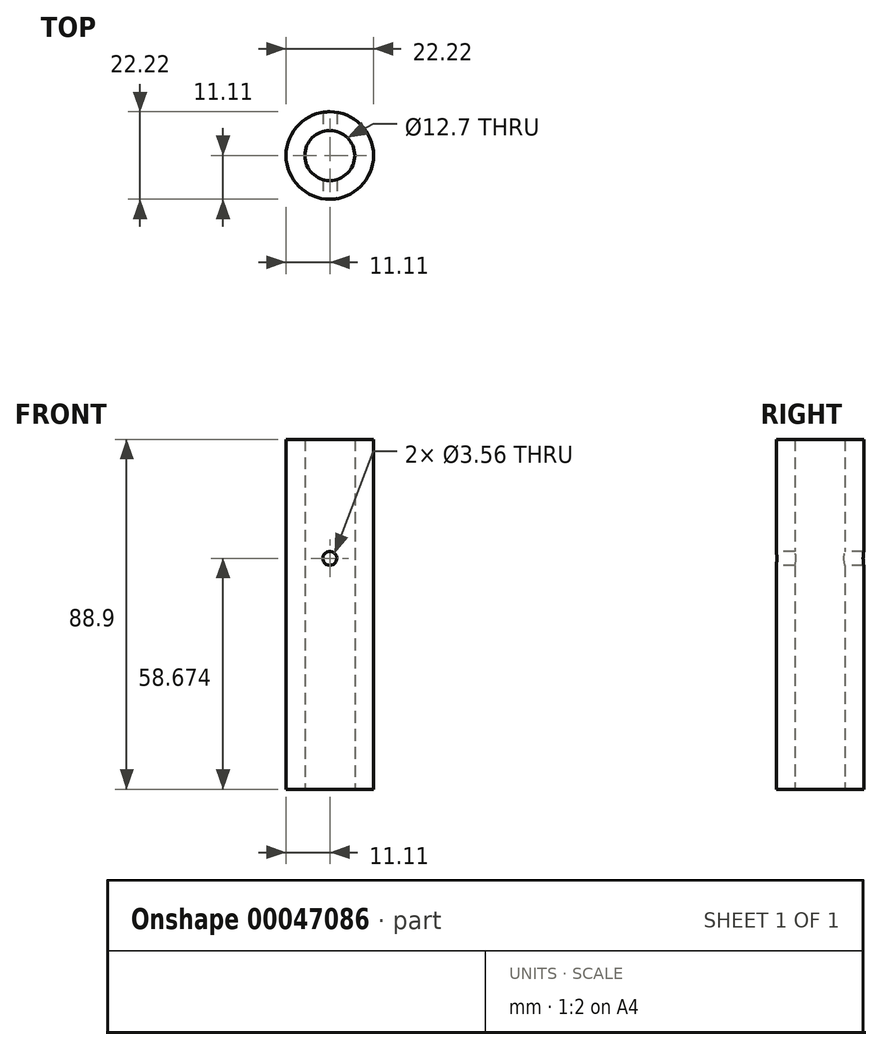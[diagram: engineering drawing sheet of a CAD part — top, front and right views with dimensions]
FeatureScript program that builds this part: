
annotation { "Feature Type Name" : "Feature", "Feature Type Description" : "" }
export const myFeature = defineFeature(function(context is Context, id is Id, definition is map)
    precondition{}
    {
        {
            var Q0;
            Q0=qCreatedBy(makeId("Top.planeOp"),FACE);
            var sketch = newSketch(context, id + "F0", { "sketchPlane" : qUnion([Q0])});
            skCircle(sketch, "E0", {"center": v(0, 0) * mm, "radius": 11.11 * mm});
            skCircle(sketch, "E1", {"center": v(0, 0) * mm, "radius": 6.35 * mm});
            skSolve(sketch);
        }
        {
            var Q0;
            Q0=makeQuery(id+"F0.imprint","IMPRINT",FACE,{"disambiguationData":[TD([[makeQuery(id+"F0.imprint","IMPRINT",EDGE,{"derivedFrom":sQuery(id+"F0.wireOp",EDGE,"E0")}),1.0]])]});
            extrude(context, id + "F1", {"entities" : qUnion([Q0]), "endBound" : BoundingType.SYMMETRIC, "depth" : 88.9 * mm});
        }
        {
            var Q0;
            Q0=qCreatedBy(makeId("Front.planeOp"),FACE);
            cPlane(context, id + "F2", {"entities" : qUnion([Q0]), "cplaneType" : CPlaneType.OFFSET, "offset" : 11.1 * mm, "width" : 152.4 * mm, "height" : 152.4 * mm});
        }
        {
            var Q0;
            Q0=qCreatedBy(id+"F2.planeOp",FACE);
            var sketch = newSketch(context, id + "F3", { "sketchPlane" : qUnion([Q0])});
            skCircle(sketch, "E2", {"center": v(0, 14.22) * mm, "radius": 1.78 * mm});
            skCircle(sketch, "E3.MirrorC", {"center": v(0, -14.22) * mm, "radius": 1.78 * mm});
            skSolve(sketch);
        }
        {
            var Q0;
            Q0=makeQuery(id+"F3.imprint","IMPRINT",FACE,{"disambiguationData":[TD([[makeQuery(id+"F3.imprint","IMPRINT",EDGE,{"derivedFrom":sQuery(id+"F3.wireOp",EDGE,"E2")}),1.0]])]});
            var Q1;
            Q1=makeQuery(id+"F3.imprint","IMPRINT",FACE,{"disambiguationData":[TD([[makeQuery(id+"F3.imprint","IMPRINT",EDGE,{"derivedFrom":sQuery(id+"F3.wireOp",EDGE,"E3.MirrorC")}),-1.0]])]});
            extrude(context, id + "F4", {"entities" : qUnion([Q0, Q1]), "operationType" : NewBodyOperationType.REMOVE, "endBound" : BoundingType.THROUGH_ALL, "oppositeDirection" : true, "depth" : 25.4 * mm});
        }
    });
